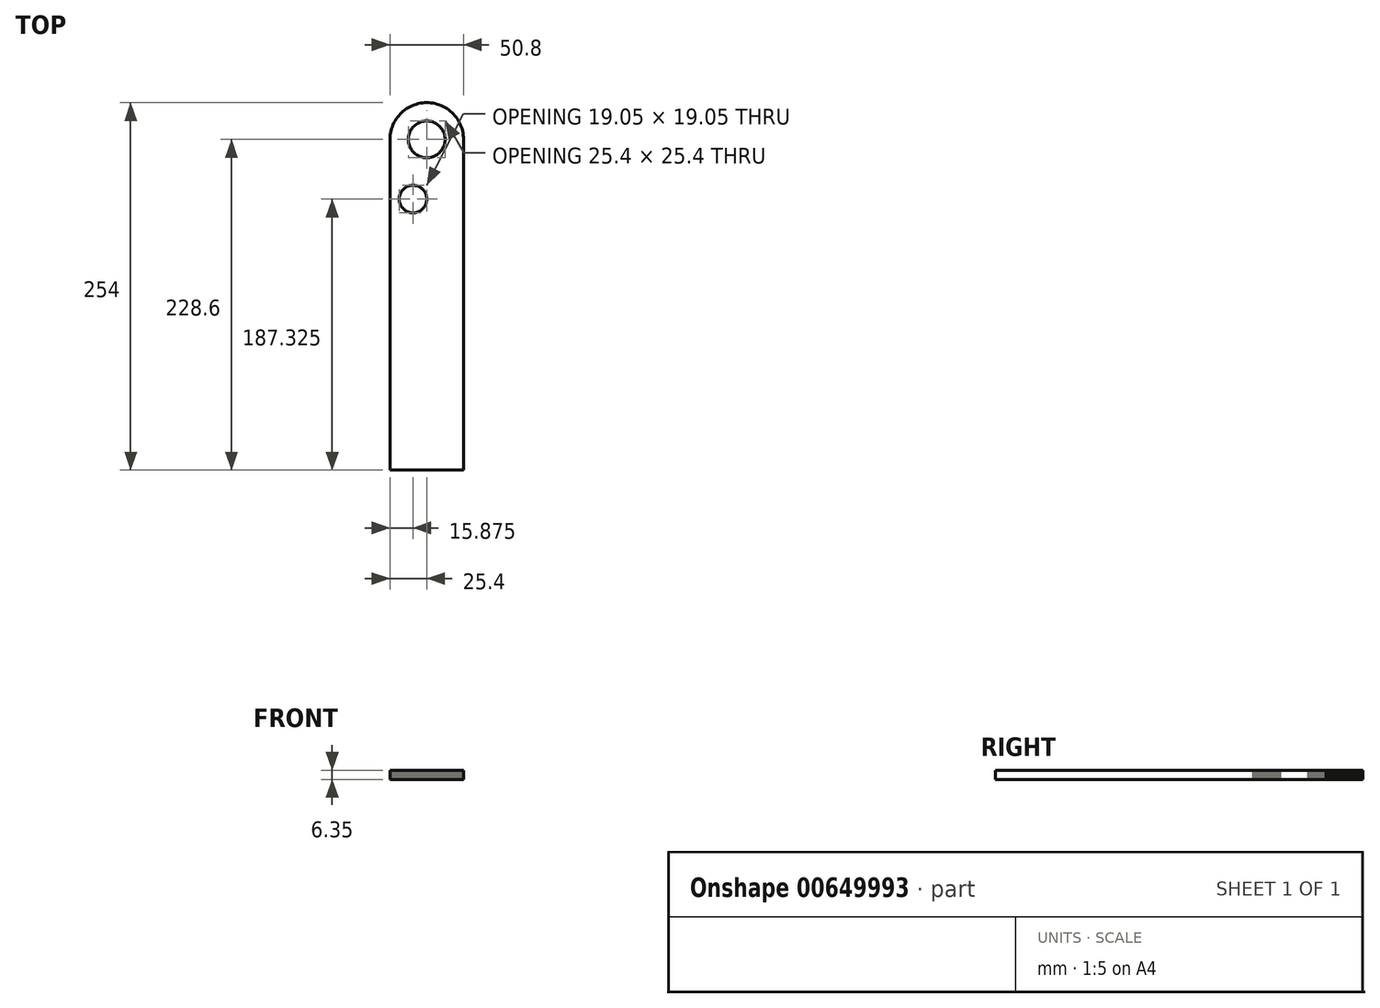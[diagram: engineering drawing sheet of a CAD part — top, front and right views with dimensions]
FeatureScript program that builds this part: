
annotation { "Feature Type Name" : "Feature", "Feature Type Description" : "" }
export const myFeature = defineFeature(function(context is Context, id is Id, definition is map)
    precondition{}
    {
        {
            var Q0;
            Q0=qCreatedBy(makeId("Top.planeOp"),FACE);
            var sketch = newSketch(context, id + "F0", { "sketchPlane" : qUnion([Q0])});
            skLineSegment(sketch, "E0", {"start": v(25.4, 101.6) * mm, "end": v(25.36, 103.08) * mm});
            skLineSegment(sketch, "E1", {"start": v(25.36, 103.08) * mm, "end": v(25.23, 104.54) * mm});
            skLineSegment(sketch, "E2", {"start": v(25.23, 104.54) * mm, "end": v(25.02, 106) * mm});
            skLineSegment(sketch, "E3", {"start": v(25.02, 106) * mm, "end": v(24.72, 107.46) * mm});
            skLineSegment(sketch, "E4", {"start": v(24.72, 107.46) * mm, "end": v(24.34, 108.88) * mm});
            skLineSegment(sketch, "E5", {"start": v(24.34, 108.88) * mm, "end": v(23.88, 110.3) * mm});
            skLineSegment(sketch, "E6", {"start": v(23.88, 110.3) * mm, "end": v(23.33, 111.65) * mm});
            skLineSegment(sketch, "E7", {"start": v(23.33, 111.65) * mm, "end": v(22.7, 113) * mm});
            skLineSegment(sketch, "E8", {"start": v(22.7, 113) * mm, "end": v(22, 114.3) * mm});
            skLineSegment(sketch, "E9", {"start": v(22, 114.3) * mm, "end": v(21.23, 115.57) * mm});
            skLineSegment(sketch, "E10", {"start": v(21.23, 115.57) * mm, "end": v(20.38, 116.78) * mm});
            skLineSegment(sketch, "E11", {"start": v(20.38, 116.78) * mm, "end": v(19.45, 117.92) * mm});
            skLineSegment(sketch, "E12", {"start": v(19.45, 117.92) * mm, "end": v(18.48, 119.04) * mm});
            skLineSegment(sketch, "E13", {"start": v(18.48, 119.04) * mm, "end": v(17.44, 120.08) * mm});
            skLineSegment(sketch, "E14", {"start": v(17.44, 120.08) * mm, "end": v(16.32, 121.05) * mm});
            skLineSegment(sketch, "E15", {"start": v(16.32, 121.05) * mm, "end": v(15.18, 121.98) * mm});
            skLineSegment(sketch, "E16", {"start": v(15.18, 121.98) * mm, "end": v(13.95, 122.83) * mm});
            skLineSegment(sketch, "E17", {"start": v(13.95, 122.83) * mm, "end": v(12.7, 123.6) * mm});
            skLineSegment(sketch, "E18", {"start": v(12.7, 123.6) * mm, "end": v(11.4, 124.3) * mm});
            skLineSegment(sketch, "E19", {"start": v(11.4, 124.3) * mm, "end": v(10.05, 124.93) * mm});
            skLineSegment(sketch, "E20", {"start": v(10.05, 124.93) * mm, "end": v(8.68, 125.48) * mm});
            skLineSegment(sketch, "E21", {"start": v(8.68, 125.48) * mm, "end": v(7.28, 125.94) * mm});
            skLineSegment(sketch, "E22", {"start": v(7.28, 125.94) * mm, "end": v(5.86, 126.32) * mm});
            skLineSegment(sketch, "E23", {"start": v(5.86, 126.32) * mm, "end": v(4.4, 126.62) * mm});
            skLineSegment(sketch, "E24", {"start": v(4.4, 126.62) * mm, "end": v(2.94, 126.83) * mm});
            skLineSegment(sketch, "E25", {"start": v(2.94, 126.83) * mm, "end": v(1.48, 126.96) * mm});
            skLineSegment(sketch, "E26", {"start": v(1.48, 126.96) * mm, "end": v(0, 127) * mm});
            skLineSegment(sketch, "E27", {"start": v(0, 127) * mm, "end": v(-1.48, 126.96) * mm});
            skLineSegment(sketch, "E28", {"start": v(-1.48, 126.96) * mm, "end": v(-2.94, 126.83) * mm});
            skLineSegment(sketch, "E29", {"start": v(-2.94, 126.83) * mm, "end": v(-4.4, 126.62) * mm});
            skLineSegment(sketch, "E30", {"start": v(-4.4, 126.62) * mm, "end": v(-5.86, 126.32) * mm});
            skLineSegment(sketch, "E31", {"start": v(-5.86, 126.32) * mm, "end": v(-7.28, 125.94) * mm});
            skLineSegment(sketch, "E32", {"start": v(-7.28, 125.94) * mm, "end": v(-8.68, 125.48) * mm});
            skLineSegment(sketch, "E33", {"start": v(-8.68, 125.48) * mm, "end": v(-10.05, 124.93) * mm});
            skLineSegment(sketch, "E34", {"start": v(-10.05, 124.93) * mm, "end": v(-11.4, 124.3) * mm});
            skLineSegment(sketch, "E35", {"start": v(-11.4, 124.3) * mm, "end": v(-12.7, 123.6) * mm});
            skLineSegment(sketch, "E36", {"start": v(-12.7, 123.6) * mm, "end": v(-13.95, 122.83) * mm});
            skLineSegment(sketch, "E37", {"start": v(-13.95, 122.83) * mm, "end": v(-15.18, 121.98) * mm});
            skLineSegment(sketch, "E38", {"start": v(-15.18, 121.98) * mm, "end": v(-16.32, 121.05) * mm});
            skLineSegment(sketch, "E39", {"start": v(-16.32, 121.05) * mm, "end": v(-17.42, 120.08) * mm});
            skLineSegment(sketch, "E40", {"start": v(-17.42, 120.08) * mm, "end": v(-18.48, 119.04) * mm});
            skLineSegment(sketch, "E41", {"start": v(-18.48, 119.04) * mm, "end": v(-19.45, 117.92) * mm});
            skLineSegment(sketch, "E42", {"start": v(-19.45, 117.92) * mm, "end": v(-20.38, 116.78) * mm});
            skLineSegment(sketch, "E43", {"start": v(-20.38, 116.78) * mm, "end": v(-21.23, 115.57) * mm});
            skLineSegment(sketch, "E44", {"start": v(-21.23, 115.57) * mm, "end": v(-22, 114.3) * mm});
            skLineSegment(sketch, "E45", {"start": v(-22, 114.3) * mm, "end": v(-22.7, 113) * mm});
            skLineSegment(sketch, "E46", {"start": v(-22.7, 113) * mm, "end": v(-23.33, 111.65) * mm});
            skLineSegment(sketch, "E47", {"start": v(-23.33, 111.65) * mm, "end": v(-23.88, 110.3) * mm});
            skLineSegment(sketch, "E48", {"start": v(-23.88, 110.3) * mm, "end": v(-24.34, 108.88) * mm});
            skLineSegment(sketch, "E49", {"start": v(-24.34, 108.88) * mm, "end": v(-24.72, 107.46) * mm});
            skLineSegment(sketch, "E50", {"start": v(-24.72, 107.46) * mm, "end": v(-25.02, 106) * mm});
            skLineSegment(sketch, "E51", {"start": v(-25.02, 106) * mm, "end": v(-25.23, 104.54) * mm});
            skLineSegment(sketch, "E52", {"start": v(-25.23, 104.54) * mm, "end": v(-25.36, 103.08) * mm});
            skLineSegment(sketch, "E53", {"start": v(-25.36, 103.08) * mm, "end": v(-25.4, 101.6) * mm});
            skLineSegment(sketch, "E54", {"start": v(-9.53, 50.8) * mm, "end": v(-8.64, 50.84) * mm});
            skLineSegment(sketch, "E55", {"start": v(-8.64, 50.84) * mm, "end": v(-7.77, 50.97) * mm});
            skLineSegment(sketch, "E56", {"start": v(-7.77, 50.97) * mm, "end": v(-6.92, 51.16) * mm});
            skLineSegment(sketch, "E57", {"start": v(-6.92, 51.16) * mm, "end": v(-6.07, 51.44) * mm});
            skLineSegment(sketch, "E58", {"start": v(-6.07, 51.44) * mm, "end": v(-5.27, 51.8) * mm});
            skLineSegment(sketch, "E59", {"start": v(-5.27, 51.8) * mm, "end": v(-4.5, 52.24) * mm});
            skLineSegment(sketch, "E60", {"start": v(-4.5, 52.24) * mm, "end": v(-3.79, 52.73) * mm});
            skLineSegment(sketch, "E61", {"start": v(-3.79, 52.73) * mm, "end": v(-3.11, 53.3) * mm});
            skLineSegment(sketch, "E62", {"start": v(-3.11, 53.3) * mm, "end": v(-2.48, 53.91) * mm});
            skLineSegment(sketch, "E63", {"start": v(-2.48, 53.91) * mm, "end": v(-1.93, 54.59) * mm});
            skLineSegment(sketch, "E64", {"start": v(-1.93, 54.59) * mm, "end": v(-1.42, 55.3) * mm});
            skLineSegment(sketch, "E65", {"start": v(-1.42, 55.3) * mm, "end": v(-1, 56.1) * mm});
            skLineSegment(sketch, "E66", {"start": v(-1, 56.1) * mm, "end": v(-0.64, 56.9) * mm});
            skLineSegment(sketch, "E67", {"start": v(-0.64, 56.9) * mm, "end": v(-0.36, 57.72) * mm});
            skLineSegment(sketch, "E68", {"start": v(-0.36, 57.72) * mm, "end": v(-0.17, 58.57) * mm});
            skLineSegment(sketch, "E69", {"start": v(-0.17, 58.57) * mm, "end": v(-0.04, 59.46) * mm});
            skLineSegment(sketch, "E70", {"start": v(-0.04, 59.46) * mm, "end": v(0, 60.33) * mm});
            skLineSegment(sketch, "E71", {"start": v(0, 60.33) * mm, "end": v(-0.04, 61.21) * mm});
            skLineSegment(sketch, "E72", {"start": v(-0.04, 61.21) * mm, "end": v(-0.17, 62.08) * mm});
            skLineSegment(sketch, "E73", {"start": v(-0.17, 62.08) * mm, "end": v(-0.36, 62.93) * mm});
            skLineSegment(sketch, "E74", {"start": v(-0.36, 62.93) * mm, "end": v(-0.64, 63.78) * mm});
            skLineSegment(sketch, "E75", {"start": v(-0.64, 63.78) * mm, "end": v(-1, 64.58) * mm});
            skLineSegment(sketch, "E76", {"start": v(-1, 64.58) * mm, "end": v(-1.42, 65.34) * mm});
            skLineSegment(sketch, "E77", {"start": v(-1.42, 65.34) * mm, "end": v(-1.93, 66.06) * mm});
            skLineSegment(sketch, "E78", {"start": v(-1.93, 66.06) * mm, "end": v(-2.48, 66.74) * mm});
            skLineSegment(sketch, "E79", {"start": v(-2.48, 66.74) * mm, "end": v(-3.11, 67.37) * mm});
            skLineSegment(sketch, "E80", {"start": v(-3.11, 67.37) * mm, "end": v(-3.79, 67.92) * mm});
            skLineSegment(sketch, "E81", {"start": v(-3.79, 67.92) * mm, "end": v(-4.5, 68.43) * mm});
            skLineSegment(sketch, "E82", {"start": v(-4.5, 68.43) * mm, "end": v(-5.27, 68.86) * mm});
            skLineSegment(sketch, "E83", {"start": v(-5.27, 68.86) * mm, "end": v(-6.07, 69.21) * mm});
            skLineSegment(sketch, "E84", {"start": v(-6.07, 69.21) * mm, "end": v(-6.92, 69.5) * mm});
            skLineSegment(sketch, "E85", {"start": v(-6.92, 69.5) * mm, "end": v(-7.77, 69.68) * mm});
            skLineSegment(sketch, "E86", {"start": v(-7.77, 69.68) * mm, "end": v(-8.64, 69.8) * mm});
            skLineSegment(sketch, "E87", {"start": v(-8.64, 69.8) * mm, "end": v(-9.53, 69.85) * mm});
            skLineSegment(sketch, "E88", {"start": v(-9.53, 69.85) * mm, "end": v(-10.4, 69.8) * mm});
            skLineSegment(sketch, "E89", {"start": v(-10.4, 69.8) * mm, "end": v(-11.28, 69.68) * mm});
            skLineSegment(sketch, "E90", {"start": v(-11.28, 69.68) * mm, "end": v(-12.13, 69.5) * mm});
            skLineSegment(sketch, "E91", {"start": v(-12.13, 69.5) * mm, "end": v(-12.98, 69.21) * mm});
            skLineSegment(sketch, "E92", {"start": v(-12.98, 69.21) * mm, "end": v(-13.78, 68.86) * mm});
            skLineSegment(sketch, "E93", {"start": v(-13.78, 68.86) * mm, "end": v(-14.54, 68.43) * mm});
            skLineSegment(sketch, "E94", {"start": v(-14.54, 68.43) * mm, "end": v(-15.26, 67.92) * mm});
            skLineSegment(sketch, "E95", {"start": v(-15.26, 67.92) * mm, "end": v(-15.94, 67.37) * mm});
            skLineSegment(sketch, "E96", {"start": v(-15.94, 67.37) * mm, "end": v(-16.57, 66.74) * mm});
            skLineSegment(sketch, "E97", {"start": v(-16.57, 66.74) * mm, "end": v(-17.12, 66.06) * mm});
            skLineSegment(sketch, "E98", {"start": v(-17.12, 66.06) * mm, "end": v(-17.63, 65.34) * mm});
            skLineSegment(sketch, "E99", {"start": v(-17.63, 65.34) * mm, "end": v(-18.06, 64.58) * mm});
            skLineSegment(sketch, "E100", {"start": v(-18.06, 64.58) * mm, "end": v(-18.41, 63.78) * mm});
            skLineSegment(sketch, "E101", {"start": v(-18.41, 63.78) * mm, "end": v(-18.7, 62.93) * mm});
            skLineSegment(sketch, "E102", {"start": v(-18.7, 62.93) * mm, "end": v(-18.88, 62.08) * mm});
            skLineSegment(sketch, "E103", {"start": v(-18.88, 62.08) * mm, "end": v(-19, 61.21) * mm});
            skLineSegment(sketch, "E104", {"start": v(-19, 61.21) * mm, "end": v(-19.05, 60.33) * mm});
            skLineSegment(sketch, "E105", {"start": v(-19.05, 60.33) * mm, "end": v(-19, 59.46) * mm});
            skLineSegment(sketch, "E106", {"start": v(-19, 59.46) * mm, "end": v(-18.88, 58.57) * mm});
            skLineSegment(sketch, "E107", {"start": v(-18.88, 58.57) * mm, "end": v(-18.7, 57.72) * mm});
            skLineSegment(sketch, "E108", {"start": v(-18.7, 57.72) * mm, "end": v(-18.41, 56.9) * mm});
            skLineSegment(sketch, "E109", {"start": v(-18.41, 56.9) * mm, "end": v(-18.06, 56.1) * mm});
            skLineSegment(sketch, "E110", {"start": v(-18.06, 56.1) * mm, "end": v(-17.63, 55.3) * mm});
            skLineSegment(sketch, "E111", {"start": v(-17.63, 55.3) * mm, "end": v(-17.12, 54.59) * mm});
            skLineSegment(sketch, "E112", {"start": v(-17.12, 54.59) * mm, "end": v(-16.57, 53.91) * mm});
            skLineSegment(sketch, "E113", {"start": v(-16.57, 53.91) * mm, "end": v(-15.94, 53.3) * mm});
            skLineSegment(sketch, "E114", {"start": v(-15.94, 53.3) * mm, "end": v(-15.26, 52.73) * mm});
            skLineSegment(sketch, "E115", {"start": v(-15.26, 52.73) * mm, "end": v(-14.54, 52.24) * mm});
            skLineSegment(sketch, "E116", {"start": v(-14.54, 52.24) * mm, "end": v(-13.78, 51.8) * mm});
            skLineSegment(sketch, "E117", {"start": v(-13.78, 51.8) * mm, "end": v(-12.98, 51.44) * mm});
            skLineSegment(sketch, "E118", {"start": v(-12.98, 51.44) * mm, "end": v(-12.13, 51.16) * mm});
            skLineSegment(sketch, "E119", {"start": v(-12.13, 51.16) * mm, "end": v(-11.28, 50.97) * mm});
            skLineSegment(sketch, "E120", {"start": v(-11.28, 50.97) * mm, "end": v(-10.4, 50.84) * mm});
            skLineSegment(sketch, "E121", {"start": v(-10.4, 50.84) * mm, "end": v(-9.53, 50.8) * mm});
            skLineSegment(sketch, "E122", {"start": v(0, 88.9) * mm, "end": v(1.06, 88.94) * mm});
            skLineSegment(sketch, "E123", {"start": v(1.06, 88.94) * mm, "end": v(2.1, 89.07) * mm});
            skLineSegment(sketch, "E124", {"start": v(2.1, 89.07) * mm, "end": v(3.11, 89.28) * mm});
            skLineSegment(sketch, "E125", {"start": v(3.11, 89.28) * mm, "end": v(4.13, 89.6) * mm});
            skLineSegment(sketch, "E126", {"start": v(4.13, 89.6) * mm, "end": v(5.1, 89.98) * mm});
            skLineSegment(sketch, "E127", {"start": v(5.1, 89.98) * mm, "end": v(6.05, 90.42) * mm});
            skLineSegment(sketch, "E128", {"start": v(6.05, 90.42) * mm, "end": v(6.94, 90.97) * mm});
            skLineSegment(sketch, "E129", {"start": v(6.94, 90.97) * mm, "end": v(7.81, 91.59) * mm});
            skLineSegment(sketch, "E130", {"start": v(7.81, 91.59) * mm, "end": v(8.6, 92.27) * mm});
            skLineSegment(sketch, "E131", {"start": v(8.6, 92.27) * mm, "end": v(9.33, 93) * mm});
            skLineSegment(sketch, "E132", {"start": v(9.33, 93) * mm, "end": v(10.03, 93.81) * mm});
            skLineSegment(sketch, "E133", {"start": v(10.03, 93.81) * mm, "end": v(10.63, 94.66) * mm});
            skLineSegment(sketch, "E134", {"start": v(10.63, 94.66) * mm, "end": v(11.18, 95.57) * mm});
            skLineSegment(sketch, "E135", {"start": v(11.18, 95.57) * mm, "end": v(11.62, 96.5) * mm});
            skLineSegment(sketch, "E136", {"start": v(11.62, 96.5) * mm, "end": v(12.02, 97.47) * mm});
            skLineSegment(sketch, "E137", {"start": v(12.02, 97.47) * mm, "end": v(12.32, 98.49) * mm});
            skLineSegment(sketch, "E138", {"start": v(12.32, 98.49) * mm, "end": v(12.53, 99.5) * mm});
            skLineSegment(sketch, "E139", {"start": v(12.53, 99.5) * mm, "end": v(12.66, 100.56) * mm});
            skLineSegment(sketch, "E140", {"start": v(12.66, 100.56) * mm, "end": v(12.7, 101.6) * mm});
            skLineSegment(sketch, "E141", {"start": v(12.7, 101.6) * mm, "end": v(12.66, 102.66) * mm});
            skLineSegment(sketch, "E142", {"start": v(12.66, 102.66) * mm, "end": v(12.53, 103.7) * mm});
            skLineSegment(sketch, "E143", {"start": v(12.53, 103.7) * mm, "end": v(12.32, 104.71) * mm});
            skLineSegment(sketch, "E144", {"start": v(12.32, 104.71) * mm, "end": v(12.02, 105.73) * mm});
            skLineSegment(sketch, "E145", {"start": v(12.02, 105.73) * mm, "end": v(11.62, 106.7) * mm});
            skLineSegment(sketch, "E146", {"start": v(11.62, 106.7) * mm, "end": v(11.18, 107.65) * mm});
            skLineSegment(sketch, "E147", {"start": v(11.18, 107.65) * mm, "end": v(10.63, 108.54) * mm});
            skLineSegment(sketch, "E148", {"start": v(10.63, 108.54) * mm, "end": v(10.03, 109.41) * mm});
            skLineSegment(sketch, "E149", {"start": v(10.03, 109.41) * mm, "end": v(9.33, 110.2) * mm});
            skLineSegment(sketch, "E150", {"start": v(9.33, 110.2) * mm, "end": v(8.6, 110.96) * mm});
            skLineSegment(sketch, "E151", {"start": v(8.6, 110.96) * mm, "end": v(7.81, 111.63) * mm});
            skLineSegment(sketch, "E152", {"start": v(7.81, 111.63) * mm, "end": v(6.94, 112.23) * mm});
            skLineSegment(sketch, "E153", {"start": v(6.94, 112.23) * mm, "end": v(6.05, 112.78) * mm});
            skLineSegment(sketch, "E154", {"start": v(6.05, 112.78) * mm, "end": v(5.1, 113.24) * mm});
            skLineSegment(sketch, "E155", {"start": v(5.1, 113.24) * mm, "end": v(4.13, 113.62) * mm});
            skLineSegment(sketch, "E156", {"start": v(4.13, 113.62) * mm, "end": v(3.11, 113.92) * mm});
            skLineSegment(sketch, "E157", {"start": v(3.11, 113.92) * mm, "end": v(2.1, 114.13) * mm});
            skLineSegment(sketch, "E158", {"start": v(2.1, 114.13) * mm, "end": v(1.06, 114.26) * mm});
            skLineSegment(sketch, "E159", {"start": v(1.06, 114.26) * mm, "end": v(0, 114.3) * mm});
            skLineSegment(sketch, "E160", {"start": v(0, 114.3) * mm, "end": v(-1.06, 114.26) * mm});
            skLineSegment(sketch, "E161", {"start": v(-1.06, 114.26) * mm, "end": v(-2.1, 114.13) * mm});
            skLineSegment(sketch, "E162", {"start": v(-2.1, 114.13) * mm, "end": v(-3.11, 113.92) * mm});
            skLineSegment(sketch, "E163", {"start": v(-3.11, 113.92) * mm, "end": v(-4.13, 113.62) * mm});
            skLineSegment(sketch, "E164", {"start": v(-4.13, 113.62) * mm, "end": v(-5.1, 113.24) * mm});
            skLineSegment(sketch, "E165", {"start": v(-5.1, 113.24) * mm, "end": v(-6.05, 112.78) * mm});
            skLineSegment(sketch, "E166", {"start": v(-6.05, 112.78) * mm, "end": v(-6.94, 112.23) * mm});
            skLineSegment(sketch, "E167", {"start": v(-6.94, 112.23) * mm, "end": v(-7.79, 111.63) * mm});
            skLineSegment(sketch, "E168", {"start": v(-7.79, 111.63) * mm, "end": v(-8.6, 110.96) * mm});
            skLineSegment(sketch, "E169", {"start": v(-8.6, 110.96) * mm, "end": v(-9.33, 110.2) * mm});
            skLineSegment(sketch, "E170", {"start": v(-9.33, 110.2) * mm, "end": v(-10.01, 109.41) * mm});
            skLineSegment(sketch, "E171", {"start": v(-10.01, 109.41) * mm, "end": v(-10.63, 108.54) * mm});
            skLineSegment(sketch, "E172", {"start": v(-10.63, 108.54) * mm, "end": v(-11.18, 107.65) * mm});
            skLineSegment(sketch, "E173", {"start": v(-11.18, 107.65) * mm, "end": v(-11.62, 106.7) * mm});
            skLineSegment(sketch, "E174", {"start": v(-11.62, 106.7) * mm, "end": v(-12, 105.73) * mm});
            skLineSegment(sketch, "E175", {"start": v(-12, 105.73) * mm, "end": v(-12.32, 104.71) * mm});
            skLineSegment(sketch, "E176", {"start": v(-12.32, 104.71) * mm, "end": v(-12.53, 103.7) * mm});
            skLineSegment(sketch, "E177", {"start": v(-12.53, 103.7) * mm, "end": v(-12.66, 102.66) * mm});
            skLineSegment(sketch, "E178", {"start": v(-12.66, 102.66) * mm, "end": v(-12.7, 101.6) * mm});
            skLineSegment(sketch, "E179", {"start": v(-12.7, 101.6) * mm, "end": v(-12.66, 100.56) * mm});
            skLineSegment(sketch, "E180", {"start": v(-12.66, 100.56) * mm, "end": v(-12.53, 99.5) * mm});
            skLineSegment(sketch, "E181", {"start": v(-12.53, 99.5) * mm, "end": v(-12.32, 98.49) * mm});
            skLineSegment(sketch, "E182", {"start": v(-12.32, 98.49) * mm, "end": v(-12, 97.47) * mm});
            skLineSegment(sketch, "E183", {"start": v(-12, 97.47) * mm, "end": v(-11.62, 96.5) * mm});
            skLineSegment(sketch, "E184", {"start": v(-11.62, 96.5) * mm, "end": v(-11.18, 95.57) * mm});
            skLineSegment(sketch, "E185", {"start": v(-11.18, 95.57) * mm, "end": v(-10.63, 94.66) * mm});
            skLineSegment(sketch, "E186", {"start": v(-10.63, 94.66) * mm, "end": v(-10.01, 93.81) * mm});
            skLineSegment(sketch, "E187", {"start": v(-10.01, 93.81) * mm, "end": v(-9.33, 93) * mm});
            skLineSegment(sketch, "E188", {"start": v(-9.33, 93) * mm, "end": v(-8.6, 92.27) * mm});
            skLineSegment(sketch, "E189", {"start": v(-8.6, 92.27) * mm, "end": v(-7.79, 91.59) * mm});
            skLineSegment(sketch, "E190", {"start": v(-7.79, 91.59) * mm, "end": v(-6.94, 90.97) * mm});
            skLineSegment(sketch, "E191", {"start": v(-6.94, 90.97) * mm, "end": v(-6.05, 90.42) * mm});
            skLineSegment(sketch, "E192", {"start": v(-6.05, 90.42) * mm, "end": v(-5.1, 89.98) * mm});
            skLineSegment(sketch, "E193", {"start": v(-5.1, 89.98) * mm, "end": v(-4.13, 89.6) * mm});
            skLineSegment(sketch, "E194", {"start": v(-4.13, 89.6) * mm, "end": v(-3.11, 89.28) * mm});
            skLineSegment(sketch, "E195", {"start": v(-3.11, 89.28) * mm, "end": v(-2.1, 89.07) * mm});
            skLineSegment(sketch, "E196", {"start": v(-2.1, 89.07) * mm, "end": v(-1.06, 88.94) * mm});
            skLineSegment(sketch, "E197", {"start": v(-1.06, 88.94) * mm, "end": v(0, 88.9) * mm});
            skLineSegment(sketch, "E198", {"start": v(25.4, 101.6) * mm, "end": v(25.4, -127) * mm});
            skLineSegment(sketch, "E199", {"start": v(25.4, -127) * mm, "end": v(-25.4, -127) * mm});
            skLineSegment(sketch, "E200", {"start": v(-25.4, -127) * mm, "end": v(-25.4, 101.6) * mm});
            skSolve(sketch);
        }
        {
            var Q0;
            Q0 = qSketchRegion(id + "F0", true);
            extrude(context, id + "F1", {"entities" : qUnion([Q0]), "depth" : 6.35 * mm, "offsetDistance" : 25.4 * mm});
        }
    });
